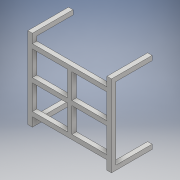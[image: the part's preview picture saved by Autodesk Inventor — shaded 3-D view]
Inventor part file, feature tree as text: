
AUTODESK INVENTOR PART (.ipt)
format: ipt  version: 2018 (Build 220112000, 112)  size: 380,928 bytes
history: native  units: mm
features: extrude x5, sketch x5
ambient origin geometry x8: Origin, YZ Plane, XZ Plane, XY Plane, X Axis, Y Axis, Z Axis, Center Point
bodies: Solid1 (feature_tree)
feature tree (10):
  extrude  "Extrusion1"  Depth=140.0mm
  extrude  "Extrusion2"  Depth=10.0mm
  extrude  "Extrusion3"  Depth=10.0mm
  extrude  "Extrusion4"  Depth=10.0mm
  extrude  "Extrusion7"  Depth=10.0mm
  sketch  "Sketch1"  dims[d0=185.0mm d1=140.0mm]
  sketch  "Sketch2"  dims[d2=10.0mm d3=10.0mm]
  sketch  "Sketch3"  dims[d4=10.0mm d5=10.0mm]
  sketch  "Sketch4"  dims[d6=5.0mm d7=10.0mm]
  sketch  "Sketch7"  dims[d8=5.0mm d9=10.0mm d10=10.0mm d11=0.0mm d12=10.0mm d13=10.0mm d14=10.0mm d15=20.0mm d16=0.0mm d17=10.0mm d18=20.0mm d19=0.0mm d20=10.0mm d21=10.0mm d22=10.0mm d23=80.0mm d24=0.0mm d40=5.0mm d41=5.0mm d42=4.8mm d45=25.0mm d46=0.0mm d47=4.8mm d48=4.8mm d49=4.8mm d50=10.0mm]
